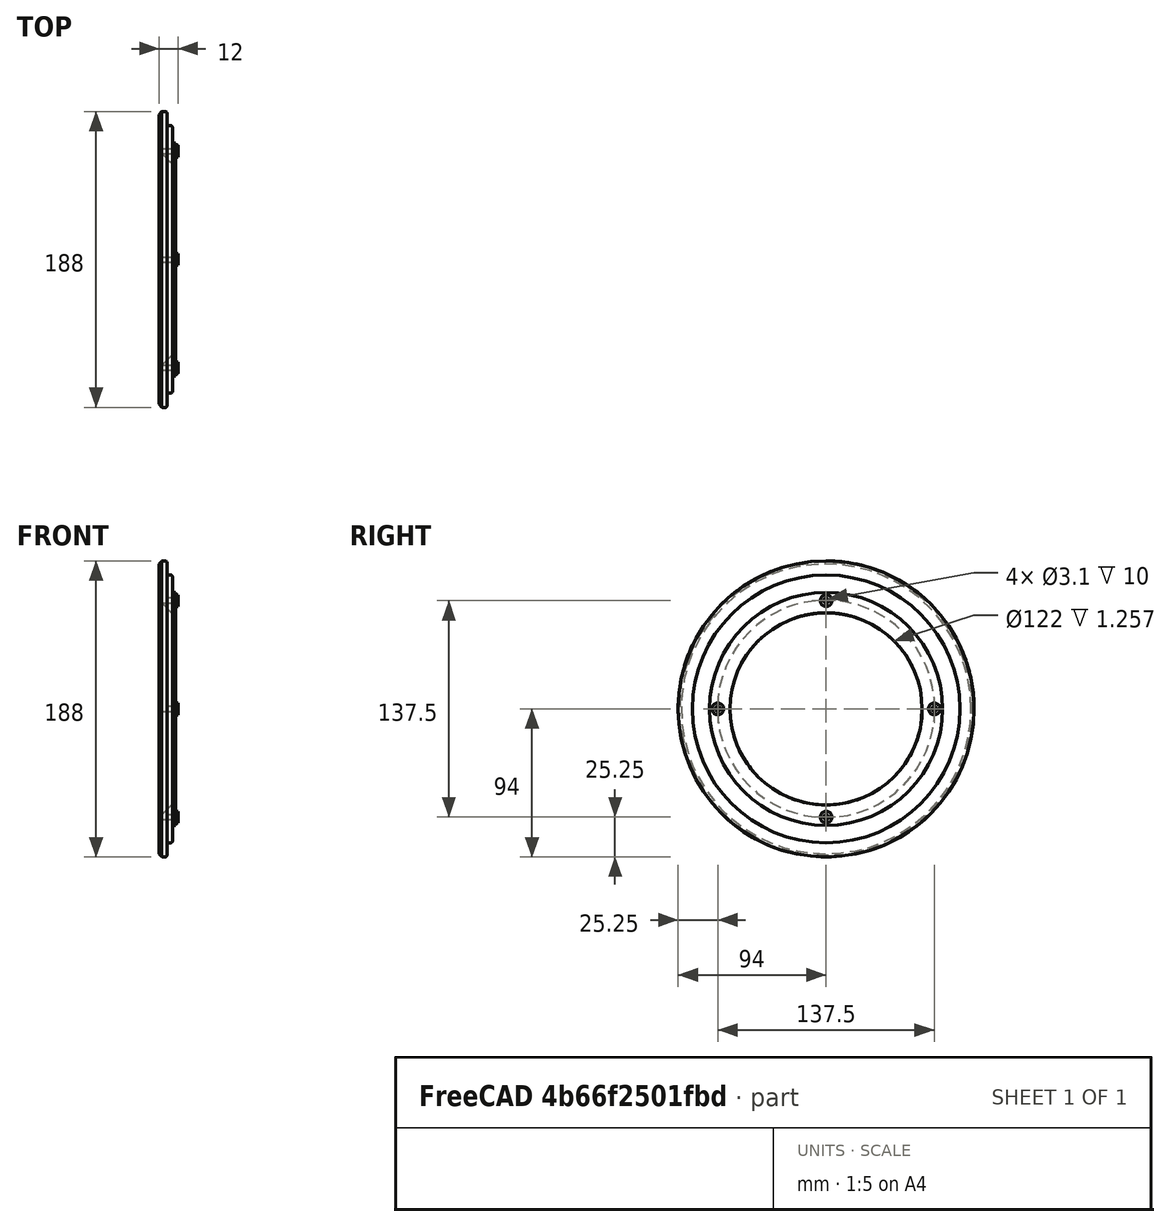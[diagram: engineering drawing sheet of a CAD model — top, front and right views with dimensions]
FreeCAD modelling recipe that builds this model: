
FCSTD DOCUMENT  (FreeCAD 0.19R)
Label: ShimanoTripleGuard2
License: All rights reserved
LicenseURL: http://en.wikipedia.org/wiki/All_rights_reserved
objects: PartDesign::Fillet×4, Sketcher::SketchObject×3, PartDesign::Chamfer×2, PartDesign::Revolution×1, PartDesign::Pad×1, PartDesign::Pocket×1, PartDesign::Body×1, Mesh::Feature×1
note: 22 computed .brp shape members not serialized (recipe doc carries the construction recipe); baked Part::Feature solids carry a one-line shape summary decoded from their .brp

FEATURE [Sketcher::SketchObject] Sketch
  FullyConstrained = true
  MapMode = 5
  Placement = pos=(0,0,0) rot=(1,0,0;1.5708rad)
  Support = -> [XZ_Plane]
  sketch-geometry (8):
    g0: LineSegment StartX=-8.5 StartY=61 StartZ=0 EndX=2 EndY=61 EndZ=0
    g1: LineSegment StartX=2 StartY=61 StartZ=0 EndX=2 EndY=74 EndZ=0
    g2: LineSegment StartX=2 StartY=74 StartZ=0 EndX=0 EndY=74 EndZ=0
    g3: LineSegment StartX=0 StartY=74 StartZ=0 EndX=0 EndY=85 EndZ=0
    g4: LineSegment StartX=0 StartY=85 StartZ=0 EndX=-3.5 EndY=85 EndZ=0
    g5: LineSegment StartX=-3.5 StartY=85 StartZ=0 EndX=-3.5 EndY=94 EndZ=0
    g6: LineSegment StartX=-3.5 StartY=94 StartZ=0 EndX=-8.5 EndY=94 EndZ=0
    g7: LineSegment StartX=-8.5 StartY=94 StartZ=0 EndX=-8.5 EndY=61 EndZ=0
  constraints (24):
    c: Horizontal(g0)
    c: Coincident(g0,g1)
    c: Coincident(g1,g2)
    c: PointOnObject(g2,g-2)
    c: Coincident(g2,g3)
    c: PointOnObject(g3,g-2)
    c: Coincident(g3,g4)
    c: Coincident(g4,g5)
    c: Coincident(g5,g6)
    c: Horizontal(g6)
    c: Coincident(g6,g7)
    c: Vertical(g7)
    c: Coincident(g0,g7)
    c: Distance(g6) = 5
    c: Horizontal(g4)
    c: Distance(g4) = 3.5
    c: Distance(g2) = 2
    c: Vertical(g1)
    c: Horizontal(g2)
    c: DistanceY(g0) = 61
    c: DistanceY(g6) = 94
    c: Vertical(g5)
    c: DistanceY(g3) = 85
    c: DistanceY(g1) = 74
FEATURE [PartDesign::Revolution] Revolution
  Angle = 360
  Axis = (1,0,0)
  Base = (0,0,0)
  Placement = pos=(0,0,0) rot=(1,0,0;1.5708rad)
  Profile = -> Sketch
  ReferenceAxis = -> Sketch [H_Axis]
FEATURE [Sketcher::SketchObject] Sketch003
  FullyConstrained = true
  MapMode = 5
  Placement = pos=(2,0,0) rot=(0.707107,0,0.707107;3.14159rad)
  Support = -> [Revolution]
  sketch-geometry (9):
    g0: LineSegment StartX=0 StartY=0 StartZ=0 EndX=106.066 EndY=106.066 EndZ=0
    g1: LineSegment StartX=1.42e-14 StartY=68.75 StartZ=0 EndX=68.75 EndY=0 EndZ=0
    g2: LineSegment StartX=68.75 StartY=0 StartZ=0 EndX=-1.42e-14 EndY=-68.75 EndZ=0
    g3: LineSegment StartX=-68.75 StartY=7.1e-15 StartZ=0 EndX=-1.42e-14 EndY=-68.75 EndZ=0
    g4: LineSegment StartX=-68.75 StartY=7.1e-15 StartZ=0 EndX=1.42e-14 EndY=68.75 EndZ=0
    g5: Circle CenterX=-68.75 CenterY=7.1e-15 CenterZ=0 NormalX=0 NormalY=0 NormalZ=1 AngleXU=0 Radius=3.7
    g6: Circle CenterX=-1.42e-14 CenterY=-68.75 CenterZ=0 NormalX=0 NormalY=0 NormalZ=1 AngleXU=0 Radius=3.7
    g7: Circle CenterX=1.42e-14 CenterY=68.75 CenterZ=0 NormalX=0 NormalY=0 NormalZ=1 AngleXU=0 Radius=3.7
    g8: Circle CenterX=68.75 CenterY=0 CenterZ=0 NormalX=0 NormalY=0 NormalZ=1 AngleXU=0 Radius=3.7
  constraints (22):
    c: Coincident(g0,g-1)
    c: Distance(g0) = 150
    c: Angle(g0) = 0.785398
    c: Coincident(g2,g1)
    c: Coincident(g3,g2)
    c: Coincident(g4,g3)
    c: Coincident(g4,g1)
    c: Equal(g3,g1)
    c: Symmetric(g1,g3,g-1)
    c: Perpendicular(g1,g4)
    c: Equal(g4,g2)
    c: Perpendicular(g1,g0)
    c: Radius(g8) = 3.7
    c: Equal(g8,g7)
    c: Equal(g8,g6)
    c: Equal(g8,g5)
    c: Coincident(g8,g1)
    c: Coincident(g7,g1)
    c: Coincident(g5,g3)
    c: Coincident(g6,g2)
    c: Equal(g2,g1)
    c: Distance(g7,g6) = 137.5
FEATURE [PartDesign::Pad] Pad
  BaseFeature = -> Revolution
  Direction = (1,1,1)
  Length = 1.5
  Length2 = 100
  Placement = pos=(0,0,0) rot=(1,0,0;1.5708rad)
  Profile = -> Sketch003
  Type = 0
FEATURE [Sketcher::SketchObject] Sketch004
  ExternalGeometry = -> [Pad]
  FullyConstrained = true
  MapMode = 5
  Placement = pos=(3.5,0,-8e-16) rot=(0.707107,0,0.707107;3.14159rad)
  Support = -> [Pad]
  sketch-geometry (4):
    g0: Circle CenterX=1.42e-14 CenterY=68.75 CenterZ=0 NormalX=0 NormalY=0 NormalZ=1 AngleXU=0 Radius=1.55
    g1: Circle CenterX=68.75 CenterY=0 CenterZ=0 NormalX=0 NormalY=0 NormalZ=1 AngleXU=0 Radius=1.55
    g2: Circle CenterX=-1.42e-14 CenterY=-68.75 CenterZ=0 NormalX=0 NormalY=0 NormalZ=1 AngleXU=0 Radius=1.55
    g3: Circle CenterX=-68.75 CenterY=7.1e-15 CenterZ=0 NormalX=0 NormalY=0 NormalZ=1 AngleXU=0 Radius=1.55
  constraints (8):
    c: Equal(g3,g2)
    c: Equal(g2,g1)
    c: Equal(g1,g0)
    c: Radius(g0) = 1.55
    c: Coincident(g3,g-3)
    c: Coincident(g2,g-5)
    c: Coincident(g1,g-4)
    c: Coincident(g0,g-6)
FEATURE [PartDesign::Pocket] Pocket
  BaseFeature = -> Pad
  Length = 10
  Length2 = 100
  Placement = pos=(0,0,0) rot=(1,0,0;1.5708rad)
  Profile = -> Sketch004
  Type = 0
FEATURE [PartDesign::Chamfer] Chamfer
  Angle = 45
  Base = -> Pocket [Edge1]
  BaseFeature = -> Pocket
  ChamferType = 0
  FlipDirection = false
  Placement = pos=(0,0,0) rot=(1,0,0;1.5708rad)
  Size = 8
  Size2 = 1
  SupportTransform = false
FEATURE [PartDesign::Chamfer] Chamfer001
  Angle = 45
  Base = -> Chamfer [Edge11]
  BaseFeature = -> Chamfer
  ChamferType = 0
  FlipDirection = false
  Placement = pos=(0,0,0) rot=(1,0,0;1.5708rad)
  Size = 2
  Size2 = 1
  SupportTransform = false
FEATURE [PartDesign::Fillet] Fillet
  Base = -> Chamfer001 [Edge17]
  BaseFeature = -> Chamfer001
  Placement = pos=(0,0,0) rot=(1,0,0;1.5708rad)
  Radius = 1
  SupportTransform = false
FEATURE [PartDesign::Fillet] Fillet001
  Base = -> Fillet [Edge6]
  BaseFeature = -> Fillet
  Placement = pos=(0,0,0) rot=(1,0,0;1.5708rad)
  Radius = 1
  SupportTransform = false
FEATURE [PartDesign::Fillet] Fillet002
  Base = -> Fillet001 [Edge18]
  BaseFeature = -> Fillet001
  Placement = pos=(0,0,0) rot=(1,0,0;1.5708rad)
  Radius = 3
  SupportTransform = false
FEATURE [PartDesign::Fillet] Fillet003
  Base = -> Fillet002 [Edge10]
  BaseFeature = -> Fillet002
  Placement = pos=(0,0,0) rot=(1,0,0;1.5708rad)
  Radius = 1
  SupportTransform = false
FEATURE [PartDesign::Body] Body
  Group = -> [Sketch,Revolution,Sketch003,Pad,Sketch004,Pocket,Chamfer,Chamfer001,Fillet,Fillet001,Fillet002,Fillet003]
  Origin = -> Origin
  Tip = -> Fillet003
FEATURE [Mesh::Feature] Mesh  label="Fillet003 (Meshed)"
